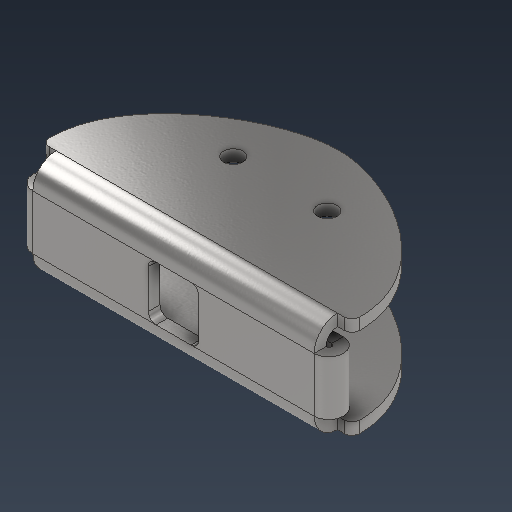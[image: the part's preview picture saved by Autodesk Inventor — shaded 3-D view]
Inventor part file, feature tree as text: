
AUTODESK INVENTOR PART (.ipt)
format: ipt  version: 2021 (Build 250183000, 183)  size: 348,672 bytes
history: native  units: mm
features: sheet_metal_op x9, sketch x9, other x8, fillet x2, hole x1
ambient origin geometry x8: Origin, YZ Plane, XZ Plane, XY Plane, X Axis, Y Axis, Z Axis, Center Point
bodies: Solid1 (feature_tree)
feature tree (29):
  sheet_metal_op  "Face1"
  sheet_metal_op  "Flange1"
  sheet_metal_op  "Flange2"
  sketch  "Sketch4"  dims[d9=6.0mm]
  sheet_metal_op  "Hem1"
  sheet_metal_op  "Hem2"
  hole  "Hole1"  [1 undecoded]
  fillet  "Fillet1"  Radius=42.5mm
  fillet  "Fillet2"  Radius=3.0mm
  other  "midPlane"
  other  "lateralPlane"
  sketch  "Sketch1"  dims[d0=80.0mm d1=40.0mm d2=6.659836mm d5=42.5mm d6=3.0mm]
  other  "Plate1"
  sketch  "Sketch2"  dims[d7=3.0mm]
  other  "Plate2"
  sheet_metal_op  "Bend1"
  sheet_metal_op  "Corner1"
  sketch  "Sketch3"  dims[d8=1.5mm]
  other  "Plate3"
  sheet_metal_op  "Bend2"
  sheet_metal_op  "Corner2"
  sketch  "Sketch7"  dims[d14=12.0mm]
  sketch  "Sketch8"  dims[d15=3.0mm]
  sketch  "Sketch9"  dims[d16=3.0mm d17=3.0mm d18=1.5mm d19=6.0mm d20=3.0mm d21=42.5mm d22=90.0deg d23=3.0mm d24=12.0mm d25=3.0mm d26=3.0mm d27=3.0mm d28=1.5mm d29=6.0mm d30=3.0mm d34=3.0mm d35=1.5mm d36=6.0mm d37=3.0mm d43=3.0mm d44=0.0mm d45=3.0mm d46=0.0mm d47=12.113mm d48=12.113mm d49=27.5mm d50=27.5mm d51=5.0mm d52=6.0mm d53=4.0mm d54=2.0mm d55=90.0deg d56=3.0mm d57=20.594885mm d58=12.0mm d59=1.5mm d60=0.75mm d61=12.0mm d62=1.5mm d63=0.75mm d64=2.0mm d65=3.0mm d66=0.0mm d67=2.0mm d68=14.0mm d69=13.0mm d70=6.5mm d71=26.0mm d72=6.0mm]
  other  "Cut2"
  other  "Cut3"
  other  "Cut4"
  sketch  "Sketch5"  dims[d10=3.0mm]
  sketch  "Sketch6"  dims[d11=26.0mm d12=90.0deg d13=3.0mm]
note: 1 required parameter value undecoded (feature->parameter linkage not recoverable at this tier; creation-order binding heuristic only, values carry confidence <= 0.55)
